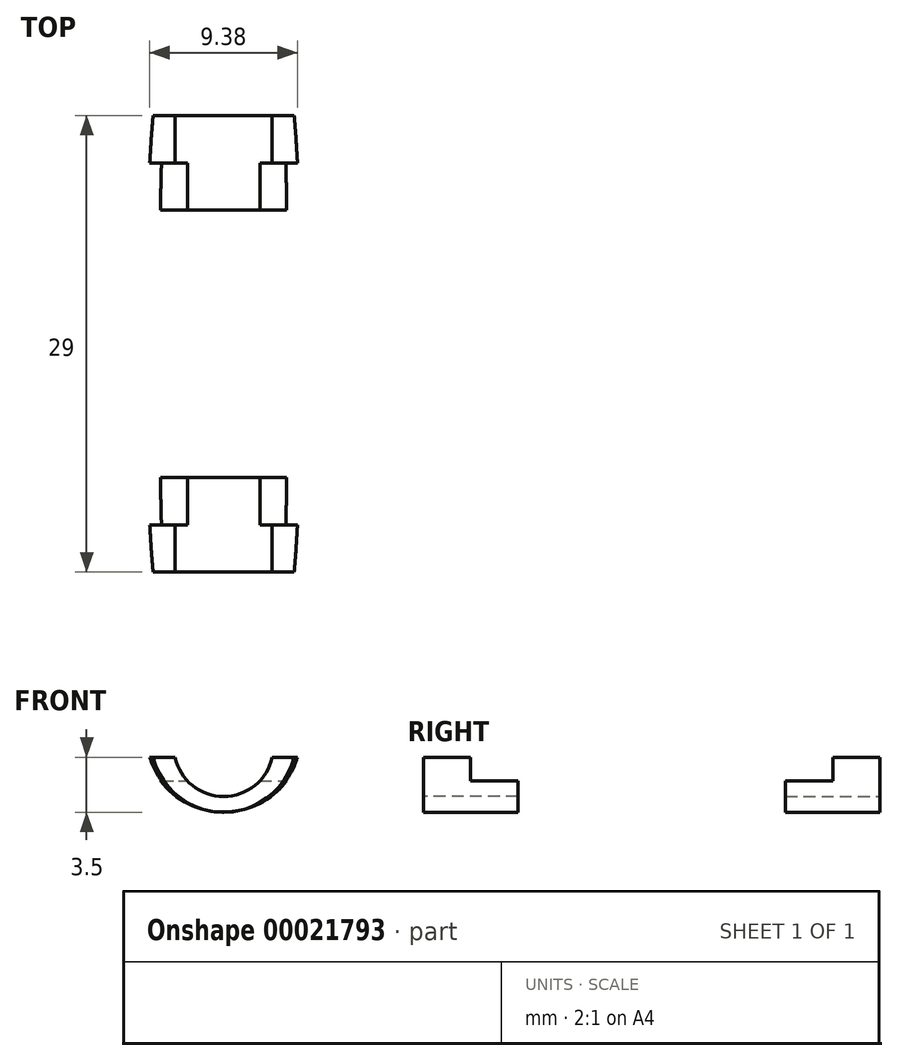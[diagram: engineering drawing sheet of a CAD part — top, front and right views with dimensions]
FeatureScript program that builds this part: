
annotation { "Feature Type Name" : "Feature", "Feature Type Description" : "" }
export const myFeature = defineFeature(function(context is Context, id is Id, definition is map)
    precondition{}
    {
        {
            var Q0;
            Q0=qCreatedBy(makeId("Top.planeOp"),FACE);
            var sketch = newSketch(context, id + "F0", { "sketchPlane" : qUnion([Q0])});
            skLineSegment(sketch, "E0.bottom", {"start": v(-2.4, 0) * mm, "end": v(2.4, 0) * mm, "construction": true});
            skLineSegment(sketch, "E0.top", {"start": v(-2.4, 4.6) * mm, "end": v(2.4, 4.6) * mm, "construction": true});
            skLineSegment(sketch, "E0.left", {"start": v(-2.4, 0) * mm, "end": v(-2.4, 4.6) * mm, "construction": true});
            skLineSegment(sketch, "E0.right", {"start": v(2.4, 0) * mm, "end": v(2.4, 4.6) * mm, "construction": true});
            skLineSegment(sketch, "E1", {"start": v(-1.27, 0) * mm, "end": v(-2, -1.5) * mm, "construction": true});
            skLineSegment(sketch, "E2", {"start": v(-2, -1.5) * mm, "end": v(-2, -14) * mm, "construction": true});
            skLineSegment(sketch, "E3", {"start": v(0, 0) * mm, "end": v(0, -14) * mm, "construction": true});
            skLineSegment(sketch, "E4", {"start": v(1.27, 0) * mm, "end": v(2, -1.5) * mm, "construction": true});
            skLineSegment(sketch, "E5", {"start": v(2, -1.5) * mm, "end": v(2, -14) * mm, "construction": true});
            skSolve(sketch);
        }
        {
            var Q0;
            Q0=qCreatedBy(makeId("Top.planeOp"),FACE);
            var sketch = newSketch(context, id + "F1", { "sketchPlane" : qUnion([Q0])});
            skLineSegment(sketch, "E6", {"start": v(2.4, -2.5) * mm, "end": v(1.6, -2.5) * mm});
            skLineSegment(sketch, "E7", {"start": v(1.6, -2.5) * mm, "end": v(1.6, -3.3) * mm});
            skLineSegment(sketch, "E8", {"start": v(1.6, -3.3) * mm, "end": v(0.4, -3.3) * mm});
            skLineSegment(sketch, "E9", {"start": v(0.4, -3.3) * mm, "end": v(0.4, -6.25) * mm});
            skLineSegment(sketch, "E10", {"start": v(0.4, -6.25) * mm, "end": v(-0.4, -6.25) * mm});
            skLineSegment(sketch, "E11", {"start": v(-0.4, -6.25) * mm, "end": v(-0.4, -7.05) * mm});
            skLineSegment(sketch, "E12", {"start": v(-0.4, -7.05) * mm, "end": v(-1.6, -7.05) * mm});
            skLineSegment(sketch, "E13", {"start": v(-1.6, -7.05) * mm, "end": v(-1.6, -10) * mm});
            skLineSegment(sketch, "E14", {"start": v(-1.6, -10) * mm, "end": v(-2.4, -10) * mm});
            skPoint(sketch, "E15", {"position": v(2, -2.5) * mm});
            skPoint(sketch, "E16", {"position": v(0, -6.25) * mm});
            skPoint(sketch, "E17", {"position": v(-2, -10) * mm});
            skLineSegment(sketch, "E18", {"start": v(-2.4, -10) * mm, "end": v(-2.4, -10.8) * mm});
            skLineSegment(sketch, "E19", {"start": v(-2.4, -10.8) * mm, "end": v(-7.4, -10.8) * mm});
            skLineSegment(sketch, "E20", {"start": v(-7.4, -10.8) * mm, "end": v(-7.4, 4.6) * mm});
            skLineSegment(sketch, "E21", {"start": v(2.4, -2.5) * mm, "end": v(2.4, -1.5) * mm});
            skLineSegment(sketch, "E22", {"start": v(2.4, -1.5) * mm, "end": v(-2.4, -1.5) * mm});
            skLineSegment(sketch, "E23", {"start": v(-2.4, -1.5) * mm, "end": v(-2.4, -10) * mm});
            skLineSegment(sketch, "E24", {"start": v(-1.6, -7.05) * mm, "end": v(-1.6, -1.5) * mm});
            skLineSegment(sketch, "E25", {"start": v(-0.4, -6.25) * mm, "end": v(-0.4, -1.5) * mm});
            skLineSegment(sketch, "E26", {"start": v(0.4, -3.3) * mm, "end": v(0.4, -1.5) * mm});
            skLineSegment(sketch, "E27", {"start": v(1.6, -2.5) * mm, "end": v(1.6, -1.5) * mm});
            skLineSegment(sketch, "E28", {"start": v(2.4, -2.5) * mm, "end": v(7.4, -2.5) * mm});
            skLineSegment(sketch, "E29", {"start": v(7.4, -2.5) * mm, "end": v(7.4, 4.6) * mm});
            skLineSegment(sketch, "E30", {"start": v(-7.4, -12) * mm, "end": v(-7.4, -10.9) * mm});
            skLineSegment(sketch, "E31", {"start": v(-7.4, -10.9) * mm, "end": v(-1.5, -10.9) * mm});
            skLineSegment(sketch, "E32", {"start": v(-1.5, -10.9) * mm, "end": v(-1.5, -7.15) * mm});
            skLineSegment(sketch, "E33", {"start": v(-1.5, -7.15) * mm, "end": v(0.5, -7.15) * mm});
            skLineSegment(sketch, "E34", {"start": v(0.5, -7.15) * mm, "end": v(0.5, -3.4) * mm});
            skLineSegment(sketch, "E35", {"start": v(0.5, -3.4) * mm, "end": v(2.4, -3.4) * mm});
            skLineSegment(sketch, "E36", {"start": v(2.4, -3.4) * mm, "end": v(2.4, -2.6) * mm});
            skLineSegment(sketch, "E37", {"start": v(2.4, -2.6) * mm, "end": v(7.4, -2.6) * mm});
            skLineSegment(sketch, "E38", {"start": v(7.4, -2.6) * mm, "end": v(7.4, -12) * mm});
            skLineSegment(sketch, "E39", {"start": v(-1.5, -7.15) * mm, "end": v(-1.5, -7.05) * mm, "construction": true});
            skLineSegment(sketch, "E40", {"start": v(-1.5, -7.15) * mm, "end": v(-1.6, -7.15) * mm, "construction": true});
            skLineSegment(sketch, "E41", {"start": v(-7.4, -10.9) * mm, "end": v(-7.4, -10.8) * mm, "construction": true});
            skLineSegment(sketch, "E42", {"start": v(0.5, -3.4) * mm, "end": v(0.4, -3.4) * mm, "construction": true});
            skLineSegment(sketch, "E43", {"start": v(0.5, -3.4) * mm, "end": v(0.5, -3.3) * mm, "construction": true});
            skLineSegment(sketch, "E44", {"start": v(2.4, -2.6) * mm, "end": v(2.4, -2.5) * mm, "construction": true});
            skLineSegment(sketch, "E45", {"start": v(-2.6, -0.2) * mm, "end": v(2.6, -0.2) * mm});
            skLineSegment(sketch, "E46", {"start": v(2.6, -0.2) * mm, "end": v(2.6, 4.6) * mm});
            skLineSegment(sketch, "E47", {"start": v(-2.6, -0.2) * mm, "end": v(-2.6, 4.6) * mm});
            skLineSegment(sketch, "E48", {"start": v(-2.6, 0) * mm, "end": v(-2.4, 0) * mm, "construction": true});
            skLineSegment(sketch, "E49", {"start": v(-2.4, 0) * mm, "end": v(-2.4, -0.2) * mm, "construction": true});
            skLineSegment(sketch, "E50", {"start": v(2.6, 0) * mm, "end": v(2.4, 0) * mm, "construction": true});
            skLineSegment(sketch, "E51", {"start": v(-7.4, 4.6) * mm, "end": v(-2.6, 4.6) * mm});
            skLineSegment(sketch, "E52", {"start": v(2.6, 4.6) * mm, "end": v(7.4, 4.6) * mm});
            skLineSegment(sketch, "E53", {"start": v(-7.4, -12) * mm, "end": v(7.4, -12) * mm});
            skLineSegment(sketch, "E54", {"start": v(2.4, -1.5) * mm, "end": v(2.6, -0.2) * mm});
            skLineSegment(sketch, "E55", {"start": v(-2.4, -1.5) * mm, "end": v(-2.6, -0.2) * mm});
            skLineSegment(sketch, "E56", {"start": v(-2.6, 4.6) * mm, "end": v(2.6, 4.6) * mm});
            skLineSegment(sketch, "E57", {"start": v(-7.4, -10.9) * mm, "end": v(-7.4, -10.8) * mm});
            skLineSegment(sketch, "E58", {"start": v(7.4, -2.6) * mm, "end": v(7.4, -2.5) * mm});
            skLineSegment(sketch, "E59", {"start": v(7.4, 4.6) * mm, "end": v(7.4, 5) * mm});
            skLineSegment(sketch, "E60", {"start": v(7.4, 5) * mm, "end": v(-7.4, 5) * mm});
            skLineSegment(sketch, "E61", {"start": v(-7.4, 5) * mm, "end": v(-7.4, 4.6) * mm});
            skLineSegment(sketch, "E62", {"start": v(7.4, -3.5) * mm, "end": v(-7.4, -3.5) * mm, "construction": true});
            skLineSegment(sketch, "E63", {"start": v(0, 5) * mm, "end": v(0, -12) * mm, "construction": true});
            skPoint(sketch, "E64", {"position": v(0, -3.5) * mm});
            skSolve(sketch);
        }
        {
            var Q0;
            Q0=qCreatedBy(makeId("Front.planeOp"),FACE);
            var sketch = newSketch(context, id + "F2", { "sketchPlane" : qUnion([Q0])});
            skCircle(sketch, "E65", {"center": v(0, 0) * mm, "radius": 3.15 * mm, "construction": true});
            skLineSegment(sketch, "E66", {"start": v(-2.4, 3.25) * mm, "end": v(2.4, 3.25) * mm, "construction": true});
            skLineSegment(sketch, "E67", {"start": v(2.4, 3.25) * mm, "end": v(2.4, 4.25) * mm, "construction": true});
            skLineSegment(sketch, "E68", {"start": v(-2.4, 3.25) * mm, "end": v(-2.4, 4.25) * mm, "construction": true});
            skPoint(sketch, "E69", {"position": v(0, 3.25) * mm});
            skArc(sketch, "E70", {"start": v(2.4, 4.25) * mm, "mid": v(0, 6.85) * mm, "end": v(-2.4, 4.25) * mm, "construction": true});
            skLineSegment(sketch, "E71", {"start": v(-2.4, 4.25) * mm, "end": v(2.4, 4.25) * mm, "construction": true});
            skCircle(sketch, "E72", {"center": v(0, -1.5) * mm, "radius": 1.25 * mm});
            skCircle(sketch, "E73", {"center": v(2.75, 1) * mm, "radius": 1.25 * mm});
            skCircle(sketch, "E74", {"center": v(-2.75, 1) * mm, "radius": 1.25 * mm});
            skLineSegment(sketch, "E75", {"start": v(1.6, 5.75) * mm, "end": v(1.6, 4.25) * mm});
            skLineSegment(sketch, "E76", {"start": v(1.6, 4.25) * mm, "end": v(2.4, 4.25) * mm});
            skLineSegment(sketch, "E77", {"start": v(2.4, 4.25) * mm, "end": v(2.4, 5.75) * mm});
            skLineSegment(sketch, "E78", {"start": v(2.4, 5.75) * mm, "end": v(3.13, 5.75) * mm});
            skLineSegment(sketch, "E79", {"start": v(1.6, 5.75) * mm, "end": v(0.5, 5.75) * mm});
            skLineSegment(sketch, "E80", {"start": v(0.5, 5.75) * mm, "end": v(0.5, 4.25) * mm});
            skLineSegment(sketch, "E81", {"start": v(0.5, 4.25) * mm, "end": v(-0.4, 4.25) * mm});
            skLineSegment(sketch, "E82", {"start": v(-0.4, 4.25) * mm, "end": v(-0.4, 5.75) * mm});
            skLineSegment(sketch, "E83", {"start": v(-0.4, 5.75) * mm, "end": v(-1.5, 5.75) * mm});
            skLineSegment(sketch, "E84", {"start": v(-1.5, 5.75) * mm, "end": v(-1.5, 4.25) * mm});
            skLineSegment(sketch, "E85", {"start": v(-1.5, 4.25) * mm, "end": v(-2.4, 4.25) * mm});
            skLineSegment(sketch, "E86", {"start": v(-2.4, 4.25) * mm, "end": v(-2.4, 5.75) * mm});
            skLineSegment(sketch, "E87", {"start": v(-2.4, 5.75) * mm, "end": v(-3.13, 5.75) * mm});
            skLineSegment(sketch, "E88", {"start": v(2.75, 1) * mm, "end": v(0, 1) * mm, "construction": true});
            skLineSegment(sketch, "E89", {"start": v(0, 1) * mm, "end": v(-2.75, 1) * mm, "construction": true});
            skLineSegment(sketch, "E90", {"start": v(-2.4, 4.25) * mm, "end": v(-2.4, 2.2) * mm});
            skLineSegment(sketch, "E91", {"start": v(-1.5, 4.25) * mm, "end": v(-1.5, 1) * mm});
            skLineSegment(sketch, "E92", {"start": v(-0.4, 4.25) * mm, "end": v(-0.4, -0.32) * mm});
            skLineSegment(sketch, "E93", {"start": v(0.5, 4.25) * mm, "end": v(0.5, -0.35) * mm});
            skLineSegment(sketch, "E94", {"start": v(1.6, 4.25) * mm, "end": v(1.6, 1.49) * mm});
            skLineSegment(sketch, "E95", {"start": v(2.4, 4.25) * mm, "end": v(2.4, 2.2) * mm});
            skLineSegment(sketch, "E96", {"start": v(2.4, 5.75) * mm, "end": v(1.6, 5.75) * mm});
            skLineSegment(sketch, "E97", {"start": v(0.5, 5.75) * mm, "end": v(-0.4, 5.75) * mm});
            skLineSegment(sketch, "E98", {"start": v(-1.5, 5.75) * mm, "end": v(-2.4, 5.75) * mm});
            skLineSegment(sketch, "E99", {"start": v(-1.5, 4.25) * mm, "end": v(-0.4, 4.25) * mm});
            skLineSegment(sketch, "E100", {"start": v(0.5, 4.25) * mm, "end": v(1.6, 4.25) * mm});
            skLineSegment(sketch, "E101", {"start": v(-4.1, 5) * mm, "end": v(-4.84, 2.1) * mm});
            skLineSegment(sketch, "E102", {"start": v(4.1, 5) * mm, "end": v(4.84, 2.1) * mm});
            skArc(sketch, "E103", {"start": v(-4.84, 2.1) * mm, "mid": v(0, -4.15) * mm, "end": v(4.84, 2.1) * mm});
            skLineSegment(sketch, "E104", {"start": v(-1.14, -0.99) * mm, "end": v(-1.5, 1) * mm});
            skLineSegment(sketch, "E105", {"start": v(-1.61, 0.49) * mm, "end": v(-1.25, -1.5) * mm});
            skLineSegment(sketch, "E106", {"start": v(1.25, -1.5) * mm, "end": v(1.61, 0.49) * mm});
            skLineSegment(sketch, "E107", {"start": v(1.5, 1) * mm, "end": v(1.14, -0.99) * mm});
            skLineSegment(sketch, "E108", {"start": v(-4, 1) * mm, "end": v(-5, 1) * mm});
            skLineSegment(sketch, "E109", {"start": v(4, 1) * mm, "end": v(5, 1) * mm});
            skLineSegment(sketch, "E110", {"start": v(4, 0.9) * mm, "end": v(5, 0.9) * mm});
            skLineSegment(sketch, "E111", {"start": v(-4, 0.9) * mm, "end": v(-5, 0.9) * mm});
            skPoint(sketch, "E112.visualSharp", {"position": v(-3.9, 5.75) * mm});
            skArc(sketch, "E112.filletArc", {"start": v(-3.13, 5.75) * mm, "mid": v(-3.74, 5.54) * mm, "end": v(-4.1, 5) * mm});
            skPoint(sketch, "E113.visualSharp", {"position": v(3.9, 5.75) * mm});
            skArc(sketch, "E113.filletArc", {"start": v(4.1, 5) * mm, "mid": v(3.74, 5.54) * mm, "end": v(3.13, 5.75) * mm});
            skSolve(sketch);
        }
        {
            var Q0;
            Q0=sQuery(id+"F1.wireOp",VERTEX,"E45.end");
            var Q1;
            Q1=qCreatedBy(makeId("Front.planeOp"),FACE);
            cPlane(context, id + "F3", {"entities" : qUnion([Q0, Q1]), "cplaneType" : CPlaneType.PLANE_POINT, "offset" : 150 * mm, "width" : 150 * mm, "height" : 150 * mm});
        }
        {
            var Q0;
            Q0=qCreatedBy(makeId("Front.planeOp"),FACE);
            var Q1;
            Q1=sQuery(id+"F1.wireOp",VERTEX,"E21.end");
            cPlane(context, id + "F4", {"entities" : qUnion([Q0, Q1]), "cplaneType" : CPlaneType.PLANE_POINT, "offset" : 150 * mm, "width" : 150 * mm, "height" : 150 * mm});
        }
        {
            var Q0;
            Q0=qCreatedBy(id+"F3.planeOp",FACE);
            var sketch = newSketch(context, id + "F5", { "sketchPlane" : qUnion([Q0])});
            skLineSegment(sketch, "E114.0", {"start": v(-2.4, 3.25) * mm, "end": v(2.4, 3.25) * mm});
            skLineSegment(sketch, "E115", {"start": v(-2.4, 3.25) * mm, "end": v(-2.4, 6.25) * mm});
            skLineSegment(sketch, "E116", {"start": v(2.4, 3.25) * mm, "end": v(2.4, 6.25) * mm});
            skLineSegment(sketch, "E117", {"start": v(2.4, 6.25) * mm, "end": v(-2.4, 6.25) * mm});
            skSolve(sketch);
        }
        {
            var Q0;
            Q0=makeQuery(id+"F2.imprint","IMPRINT",FACE,{"disambiguationData":[TD([[makeQuery(id+"F2.imprint","IMPRINT",EDGE,{"derivedFrom":sQuery(id+"F2.wireOp",EDGE,"E86")}),1.0]])]});
            var Q1;
            Q1=makeQuery(id+"F2.imprint","IMPRINT",FACE,{"disambiguationData":[TD([[makeQuery(id+"F2.imprint","IMPRINT",EDGE,{"derivedFrom":sQuery(id+"F2.wireOp",EDGE,"E85")}),1.0]])]});
            var Q2;
            Q2=makeQuery(id+"F2.imprint","IMPRINT",FACE,{"disambiguationData":[TD([[makeQuery(id+"F2.imprint","IMPRINT",EDGE,{"derivedFrom":sQuery(id+"F2.wireOp",EDGE,"E82")}),1.0]])]});
            var Q3;
            Q3=makeQuery(id+"F2.imprint","IMPRINT",FACE,{"disambiguationData":[TD([[makeQuery(id+"F2.imprint","IMPRINT",EDGE,{"derivedFrom":sQuery(id+"F2.wireOp",EDGE,"E81")}),1.0]])]});
            var Q4;
            Q4=makeQuery(id+"F2.imprint","IMPRINT",FACE,{"disambiguationData":[TD([[makeQuery(id+"F2.imprint","IMPRINT",EDGE,{"derivedFrom":sQuery(id+"F2.wireOp",EDGE,"E75")}),-1.0]])]});
            var Q5;
            Q5=makeQuery(id+"F2.imprint","IMPRINT",FACE,{"disambiguationData":[TD([[makeQuery(id+"F2.imprint","IMPRINT",EDGE,{"derivedFrom":sQuery(id+"F2.wireOp",EDGE,"E76")}),-1.0]])]});
            var Q6;
            Q6=makeQuery(id+"F2.imprint","IMPRINT",FACE,{"disambiguationData":[TD([[makeQuery(id+"F2.imprint","IMPRINT",EDGE,{"derivedFrom":sQuery(id+"F2.wireOp",EDGE,"E77")}),-1.0]])]});
            var Q7;
            {var subQ3=sQuery(id+"F2.wireOp",EDGE,"41fa8a35-a4bc-480c-a0cd-76908c7cfabe");Q7=makeQuery(id+"F2.imprint","IMPRINT",FACE,{"disambiguationData":[TD([[makeQuery(id+"F2.imprint","IMPRINT",EDGE,{"derivedFrom":subQ3}),1.0]])]});}
            var Q8;
            Q8=makeQuery(id+"F2.imprint","IMPRINT",FACE,{"disambiguationData":[TD([[makeQuery(id+"F2.imprint","IMPRINT",EDGE,{"derivedFrom":sQuery(id+"F2.wireOp",EDGE,"E84")}),-1.0]])]});
            var Q9;
            Q9=makeQuery(id+"F2.imprint","IMPRINT",FACE,{"disambiguationData":[TD([[makeQuery(id+"F2.imprint","IMPRINT",EDGE,{"derivedFrom":sQuery(id+"F2.wireOp",EDGE,"E80")}),-1.0]])]});
            var Q10;
            Q10=makeQuery(id+"F2.imprint","IMPRINT",FACE,{"disambiguationData":[TD([[makeQuery(id+"F2.imprint","IMPRINT",EDGE,{"derivedFrom":sQuery(id+"F2.wireOp",EDGE,"E75")}),1.0]])]});
            var Q11;
            {var subQ2=sQuery(id+"F2.wireOp",EDGE,"E93");Q11=makeQuery(id+"F2.imprint","IMPRINT",FACE,{"disambiguationData":[TD([[makeQuery(id+"F2.imprint","IMPRINT",EDGE,{"derivedFrom":subQ2}),1.0]])]});}
            var Q12;
            {var subQ2=sQuery(id+"F2.wireOp",EDGE,"E91");Q12=makeQuery(id+"F2.imprint","IMPRINT",FACE,{"disambiguationData":[TD([[makeQuery(id+"F2.imprint","IMPRINT",EDGE,{"derivedFrom":subQ2}),1.0]])]});}
            var Q13;
            {var subQ1=sQuery(id+"F2.wireOp",EDGE,"E105");Q13=makeQuery(id+"F2.imprint","IMPRINT",FACE,{"disambiguationData":[TD([[makeQuery(id+"F2.imprint","IMPRINT",EDGE,{"derivedFrom":subQ1}),-1.0]])]});}
            extrude(context, id + "F6", {"entities" : qUnion([Q0, Q1, Q2, Q3, Q4, Q5, Q6, Q7, Q8, Q9, Q10, Q11, Q12, Q13]), "depth" : 12 * mm, "hasSecondDirection" : true, "secondDirectionOppositeDirection" : true, "secondDirectionDepth" : 5 * mm});
        }
        {
            var Q0;
            Q0=makeQuery(id+"F1.imprint","IMPRINT",FACE,{"disambiguationData":[TD([[makeQuery(id+"F1.imprint","IMPRINT",EDGE,{"derivedFrom":sQuery(id+"F1.wireOp",EDGE,"E18")}),-1.0]])]});
            var Q1;
            Q1=makeQuery(id+"F1.imprint","IMPRINT",FACE,{"disambiguationData":[TD([[makeQuery(id+"F1.imprint","IMPRINT",EDGE,{"derivedFrom":sQuery(id+"F1.wireOp",EDGE,"E13")}),-1.0]])]});
            var Q2;
            Q2=makeQuery(id+"F1.imprint","IMPRINT",FACE,{"disambiguationData":[TD([[makeQuery(id+"F1.imprint","IMPRINT",EDGE,{"derivedFrom":sQuery(id+"F1.wireOp",EDGE,"E11")}),-1.0]])]});
            var Q3;
            Q3=makeQuery(id+"F1.imprint","IMPRINT",FACE,{"disambiguationData":[TD([[makeQuery(id+"F1.imprint","IMPRINT",EDGE,{"derivedFrom":sQuery(id+"F1.wireOp",EDGE,"E9")}),-1.0]])]});
            var Q4;
            Q4=makeQuery(id+"F1.imprint","IMPRINT",FACE,{"disambiguationData":[TD([[makeQuery(id+"F1.imprint","IMPRINT",EDGE,{"derivedFrom":sQuery(id+"F1.wireOp",EDGE,"E7")}),-1.0]])]});
            var Q5;
            Q5=makeQuery(id+"F1.imprint","IMPRINT",FACE,{"disambiguationData":[TD([[makeQuery(id+"F1.imprint","IMPRINT",EDGE,{"derivedFrom":sQuery(id+"F1.wireOp",EDGE,"E6")}),-1.0]])]});
            var Q6;
            Q6=makeQuery(id+"F1.imprint","IMPRINT",FACE,{"disambiguationData":[TD([[makeQuery(id+"F1.imprint","IMPRINT",EDGE,{"derivedFrom":sQuery(id+"F1.wireOp",EDGE,"E21")}),-1.0]])]});
            var Q7;
            Q7=makeQuery(id+"F1.imprint","IMPRINT",FACE,{"disambiguationData":[TD([[makeQuery(id+"F1.imprint","IMPRINT",EDGE,{"derivedFrom":sQuery(id+"F1.wireOp",EDGE,"E45")}),-1.0]])]});
            var Q8;
            Q8=makeQuery(id+"F1.imprint","IMPRINT",FACE,{"disambiguationData":[TD([[makeQuery(id+"F1.imprint","IMPRINT",EDGE,{"derivedFrom":sQuery(id+"F1.wireOp",EDGE,"E45")}),1.0]])]});
            var Q9;
            Q9=makeQuery(id+"F1.imprint","IMPRINT",FACE,{"disambiguationData":[TD([[makeQuery(id+"F1.imprint","IMPRINT",EDGE,{"derivedFrom":sQuery(id+"F1.wireOp",EDGE,"E30")}),-1.0]])]});
            var Q10;
            Q10=makeQuery(id+"F1.imprint","IMPRINT",FACE,{"disambiguationData":[TD([[makeQuery(id+"F1.imprint","IMPRINT",EDGE,{"derivedFrom":sQuery(id+"F1.wireOp",EDGE,"E51")}),1.0]])]});
            extrude(context, id + "F7", {"entities" : qUnion([Q0, Q1, Q2, Q3, Q4, Q5, Q6, Q7, Q8, Q9, Q10]), "operationType" : NewBodyOperationType.INTERSECT, "depth" : 25 * mm, "hasSecondDirection" : true, "secondDirectionOppositeDirection" : true, "secondDirectionDepth" : 25 * mm});
        }
        {
            var Q0;
            Q0=makeQuery(id+"F2.imprint","IMPRINT",FACE,{"disambiguationData":[TD([[makeQuery(id+"F2.imprint","IMPRINT",EDGE,{"derivedFrom":sQuery(id+"F2.wireOp",EDGE,"E84")}),-1.0]])]});
            var Q1;
            Q1=makeQuery(id+"F2.imprint","IMPRINT",FACE,{"disambiguationData":[TD([[makeQuery(id+"F2.imprint","IMPRINT",EDGE,{"derivedFrom":sQuery(id+"F2.wireOp",EDGE,"E80")}),-1.0]])]});
            var Q2;
            Q2=makeQuery(id+"F2.imprint","IMPRINT",FACE,{"disambiguationData":[TD([[makeQuery(id+"F2.imprint","IMPRINT",EDGE,{"derivedFrom":sQuery(id+"F2.wireOp",EDGE,"E75")}),1.0]])]});
            var Q3;
            Q3=qCreatedBy(id+"F3.planeOp",FACE);
            extrude(context, id + "F8", {"entities" : qUnion([Q0, Q1, Q2]), "operationType" : NewBodyOperationType.REMOVE, "endBoundEntityFace" : qUnion([Q3]), "depth" : 25 * mm});
        }
        {
            var Q0;
            Q0=makeQuery(id+"F2.imprint","IMPRINT",FACE,{"disambiguationData":[TD([[makeQuery(id+"F2.imprint","IMPRINT",EDGE,{"derivedFrom":sQuery(id+"F2.wireOp",EDGE,"E84")}),-1.0]])]});
            var Q1;
            Q1=makeQuery(id+"F2.imprint","IMPRINT",FACE,{"disambiguationData":[TD([[makeQuery(id+"F2.imprint","IMPRINT",EDGE,{"derivedFrom":sQuery(id+"F2.wireOp",EDGE,"E82")}),1.0]])]});
            var Q2;
            Q2=makeQuery(id+"F2.imprint","IMPRINT",FACE,{"disambiguationData":[TD([[makeQuery(id+"F2.imprint","IMPRINT",EDGE,{"derivedFrom":sQuery(id+"F2.wireOp",EDGE,"E80")}),-1.0]])]});
            var Q3;
            Q3=makeQuery(id+"F2.imprint","IMPRINT",FACE,{"disambiguationData":[TD([[makeQuery(id+"F2.imprint","IMPRINT",EDGE,{"derivedFrom":sQuery(id+"F2.wireOp",EDGE,"E75")}),-1.0]])]});
            var Q4;
            Q4=makeQuery(id+"F2.imprint","IMPRINT",FACE,{"disambiguationData":[TD([[makeQuery(id+"F2.imprint","IMPRINT",EDGE,{"derivedFrom":sQuery(id+"F2.wireOp",EDGE,"E75")}),1.0]])]});
            var Q5;
            Q5=qCreatedBy(id+"F4.planeOp",FACE);
            extrude(context, id + "F9", {"entities" : qUnion([Q0, Q1, Q2, Q3, Q4]), "operationType" : NewBodyOperationType.REMOVE, "endBound" : BoundingType.UP_TO_SURFACE, "endBoundEntityFace" : qUnion([Q5]), "depth" : 25 * mm});
        }
        {
            var Q0;
            Q0 = qSketchRegion(id + "F5", true);
            extrude(context, id + "F10", {"entities" : qUnion([Q0]), "operationType" : NewBodyOperationType.REMOVE, "oppositeDirection" : true, "depth" : 25 * mm});
        }
        {
            var Q0;
            {var subQ0=sQuery(id+"F2.wireOp",EDGE,"E76");var subQ1=sQuery(id+"F2.wireOp",EDGE,"E81");var subQ2=sQuery(id+"F2.wireOp",EDGE,"E85");Q0=makeQuery(id+"F10.boolean.opBoolean","INTERSECT",EDGE,{"derivedFrom":[makeQuery(id+"F9.boolean.opBoolean","MERGE",FACE,{"derivedFrom":[makeQuery(id+"F8.boolean.opBoolean","COPY",FACE,{"derivedFrom":makeQuery(id+"F8.opExtrude","SWEPT_FACE",FACE,{"disambiguationData":[OSD([subQ0])]})}),makeQuery(id+"F8.boolean.opBoolean","COPY",FACE,{"derivedFrom":makeQuery(id+"F8.opExtrude","SWEPT_FACE",FACE,{"disambiguationData":[OSD([subQ1])]})}),makeQuery(id+"F8.boolean.opBoolean","COPY",FACE,{"derivedFrom":makeQuery(id+"F8.opExtrude","SWEPT_FACE",FACE,{"disambiguationData":[OSD([subQ2])]})}),makeQuery(id+"F9.opExtrude","SWEPT_FACE",FACE,{"disambiguationData":[OSD([subQ0,subQ1,subQ2,sQuery(id+"F2.wireOp",EDGE,"E99"),sQuery(id+"F2.wireOp",EDGE,"E100")])]})]}),makeQuery(id+"F10.opExtrude","CAP_FACE",FACE,{"disambiguationData":[OSD([sQuery(id+"F5.wireOp",EDGE,"E114.0"),sQuery(id+"F5.wireOp",EDGE,"E115"),sQuery(id+"F5.wireOp",EDGE,"E116"),sQuery(id+"F5.wireOp",EDGE,"E117")])],"isStart":true})]});}
            chamfer(context, id + "F11", {"entities" : qUnion([Q0]), "chamferType" : ChamferType.OFFSET_ANGLE, "width" : 1.5 * mm, "oppositeDirection" : true, "angle" : 30 * degree, "tangentPropagation" : true});
        }
        {
            var Q0;
            Q0=makeQuery(id+"F9.boolean.opBoolean","COPY",EDGE,{"disambiguationData":[OD(0.0)],"derivedFrom":makeQuery(id+"F9.opExtrude","CAP_EDGE",EDGE,{"disambiguationData":[OSD([sQuery(id+"F2.wireOp",EDGE,"E79"),sQuery(id+"F2.wireOp",EDGE,"E83"),sQuery(id+"F2.wireOp",EDGE,"E96"),sQuery(id+"F2.wireOp",EDGE,"E97"),sQuery(id+"F2.wireOp",EDGE,"E98")])],"isStart":false})});
            var Q1;
            Q1=makeQuery(id+"F9.boolean.opBoolean","COPY",EDGE,{"disambiguationData":[OD(1.0)],"derivedFrom":makeQuery(id+"F9.opExtrude","CAP_EDGE",EDGE,{"disambiguationData":[OSD([sQuery(id+"F2.wireOp",EDGE,"E79"),sQuery(id+"F2.wireOp",EDGE,"E83"),sQuery(id+"F2.wireOp",EDGE,"E96"),sQuery(id+"F2.wireOp",EDGE,"E97"),sQuery(id+"F2.wireOp",EDGE,"E98")])],"isStart":false})});
            chamfer(context, id + "F12", {"entities" : qUnion([Q0, Q1]), "chamferType" : ChamferType.OFFSET_ANGLE, "width" : 1.5 * mm, "oppositeDirection" : true, "angle" : 30 * degree, "tangentPropagation" : true});
        }
        {
            var Q0;
            Q0=makeQuery(id+"F6.opExtrude","CAP_FACE",FACE,{"disambiguationData":[OSD([sQuery(id+"F2.wireOp",EDGE,"E72"),sQuery(id+"F2.wireOp",EDGE,"E73"),sQuery(id+"F2.wireOp",EDGE,"E74"),sQuery(id+"F2.wireOp",EDGE,"E78"),sQuery(id+"F2.wireOp",EDGE,"E79"),sQuery(id+"F2.wireOp",EDGE,"E83"),sQuery(id+"F2.wireOp",EDGE,"E87"),sQuery(id+"F2.wireOp",EDGE,"E96"),sQuery(id+"F2.wireOp",EDGE,"E97"),sQuery(id+"F2.wireOp",EDGE,"E98"),sQuery(id+"F2.wireOp",EDGE,"E101"),sQuery(id+"F2.wireOp",EDGE,"E102"),sQuery(id+"F2.wireOp",EDGE,"E103"),sQuery(id+"F2.wireOp",EDGE,"E104"),sQuery(id+"F2.wireOp",EDGE,"E107"),sQuery(id+"F2.wireOp",EDGE,"E108"),sQuery(id+"F2.wireOp",EDGE,"E109")])],"isStart":false});
            cPlane(context, id + "F13", {"entities" : qUnion([Q0]), "cplaneType" : CPlaneType.OFFSET, "offset" : 0 * mm, "width" : 150 * mm, "height" : 150 * mm});
        }
        {
            var Q0;
            Q0=qCreatedBy(id+"F13.planeOp",FACE);
            var sketch = newSketch(context, id + "F14", { "sketchPlane" : qUnion([Q0])});
            skCircle(sketch, "E118.0", {"center": v(2.75, 1) * mm, "radius": 1.25 * mm, "construction": true});
            skCircle(sketch, "E119.0", {"center": v(0, -1.5) * mm, "radius": 1.25 * mm, "construction": true});
            skCircle(sketch, "E120.0", {"center": v(-2.75, 1) * mm, "radius": 1.25 * mm, "construction": true});
            skLineSegment(sketch, "E121", {"start": v(-3.6, 0.08) * mm, "end": v(-0.84, -2.42) * mm});
            skLineSegment(sketch, "E122", {"start": v(0.84, -2.42) * mm, "end": v(3.6, 0.08) * mm});
            skLineSegment(sketch, "E123", {"start": v(2.75, 2.25) * mm, "end": v(-2.75, 2.25) * mm});
            skArc(sketch, "E124", {"start": v(-2.75, 2.25) * mm, "mid": v(-3.92, 1.45) * mm, "end": v(-3.6, 0.08) * mm});
            skArc(sketch, "E125", {"start": v(-0.84, -2.42) * mm, "mid": v(0, -2.75) * mm, "end": v(0.84, -2.42) * mm});
            skArc(sketch, "E126", {"start": v(3.6, 0.08) * mm, "mid": v(3.92, 1.45) * mm, "end": v(2.75, 2.25) * mm});
            skSolve(sketch);
        }
        {
            var Q0;
            Q0=makeQuery(id+"F6.opExtrude","CAP_FACE",FACE,{"disambiguationData":[OSD([sQuery(id+"F2.wireOp",EDGE,"E72"),sQuery(id+"F2.wireOp",EDGE,"E73"),sQuery(id+"F2.wireOp",EDGE,"E74"),sQuery(id+"F2.wireOp",EDGE,"E103"),sQuery(id+"F2.wireOp",EDGE,"E105"),sQuery(id+"F2.wireOp",EDGE,"E106"),sQuery(id+"F2.wireOp",EDGE,"E110"),sQuery(id+"F2.wireOp",EDGE,"E111")])],"isStart":false});
            cPlane(context, id + "F15", {"entities" : qUnion([Q0]), "cplaneType" : CPlaneType.OFFSET, "offset" : 6 * mm, "width" : 150 * mm, "height" : 150 * mm});
        }
        {
            var Q0;
            Q0=qCreatedBy(id+"F15.planeOp",FACE);
            var sketch = newSketch(context, id + "F16", { "sketchPlane" : qUnion([Q0])});
            skCircle(sketch, "E127.0", {"center": v(0, -1.5) * mm, "radius": 1.25 * mm, "construction": true});
            skArc(sketch, "E128", {"start": v(1.25, -1.25) * mm, "mid": v(2.5, 0) * mm, "end": v(1.25, 1.25) * mm});
            skArc(sketch, "E129", {"start": v(-1.25, 1.25) * mm, "mid": v(-2.5, 0) * mm, "end": v(-1.25, -1.25) * mm});
            skLineSegment(sketch, "E130", {"start": v(-1.25, 1.25) * mm, "end": v(1.25, 1.25) * mm});
            skLineSegment(sketch, "E131", {"start": v(1.25, -1.25) * mm, "end": v(1.05, -1.25) * mm});
            skLineSegment(sketch, "E132", {"start": v(-1.05, -1.25) * mm, "end": v(-1.25, -1.25) * mm});
            skLineSegment(sketch, "E133", {"start": v(1.05, -1.25) * mm, "end": v(-1.05, -1.25) * mm});
            skSolve(sketch);
        }
        {
            var Q0;
            Q0=qCreatedBy(id+"F15.planeOp",FACE);
            var sketch = newSketch(context, id + "F17", { "sketchPlane" : qUnion([Q0])});
            skCircle(sketch, "E134", {"center": v(0, 0) * mm, "radius": 3.15 * mm});
            skSolve(sketch);
        }
        {
            var Q0;
            Q0=qCreatedBy(id+"F15.planeOp",FACE);
            cPlane(context, id + "F18", {"entities" : qUnion([Q0]), "cplaneType" : CPlaneType.OFFSET, "offset" : 4 * mm, "width" : 150 * mm, "height" : 150 * mm});
        }
        {
            var Q0;
            Q0=qCreatedBy(id+"F13.planeOp",FACE);
            var sketch = newSketch(context, id + "F19", { "sketchPlane" : qUnion([Q0])});
            skArc(sketch, "E135.0", {"start": v(-4.84, 2.1) * mm, "mid": v(0, -4.15) * mm, "end": v(4.84, 2.1) * mm});
            skLineSegment(sketch, "E136.0", {"start": v(-4.1, 5) * mm, "end": v(-4.84, 2.1) * mm});
            skArc(sketch, "E137.0", {"start": v(-3.13, 5.75) * mm, "mid": v(-3.74, 5.54) * mm, "end": v(-4.1, 5) * mm});
            skArc(sketch, "E138.0", {"start": v(4.1, 5) * mm, "mid": v(3.74, 5.54) * mm, "end": v(3.13, 5.75) * mm});
            skLineSegment(sketch, "E139.0", {"start": v(4.1, 5) * mm, "end": v(4.84, 2.1) * mm});
            skLineSegment(sketch, "E140", {"start": v(3.13, 5.75) * mm, "end": v(-3.13, 5.75) * mm});
            skSolve(sketch);
        }
        {
            var Q0;
            Q0=qCreatedBy(id+"F18.planeOp",FACE);
            var sketch = newSketch(context, id + "F20", { "sketchPlane" : qUnion([Q0])});
            skArc(sketch, "E141", {"start": v(-3.8, 1.66) * mm, "mid": v(3.06, -2.8) * mm, "end": v(-1.98, 3.65) * mm});
            skArc(sketch, "E142", {"start": v(-2.63, 3.21) * mm, "mid": v(-3.3, 2.5) * mm, "end": v(-3.8, 1.66) * mm});
            skArc(sketch, "E143", {"start": v(-1.98, 3.65) * mm, "mid": v(-2.32, 3.44) * mm, "end": v(-2.63, 3.21) * mm});
            skLineSegment(sketch, "E144", {"start": v(-1.98, 3.65) * mm, "end": v(0, 0) * mm, "construction": true});
            skLineSegment(sketch, "E145", {"start": v(-2.63, 3.21) * mm, "end": v(0, 0) * mm, "construction": true});
            skLineSegment(sketch, "E146", {"start": v(-3.8, 1.66) * mm, "end": v(0, 0) * mm, "construction": true});
            skLineSegment(sketch, "E147.MirrorCS", {"start": v(1.98, 3.65) * mm, "end": v(0, 0) * mm, "construction": true});
            skLineSegment(sketch, "E148.MirrorCS", {"start": v(2.63, 3.21) * mm, "end": v(0, 0) * mm, "construction": true});
            skLineSegment(sketch, "E149.MirrorCS", {"start": v(3.8, 1.66) * mm, "end": v(0, 0) * mm, "construction": true});
            skSolve(sketch);
        }
        {
            var Q0;
            Q0=makeQuery(id+"F19.imprint","IMPRINT",FACE,{"disambiguationData":[TD([[makeQuery(id+"F19.imprint","IMPRINT",EDGE,{"derivedFrom":sQuery(id+"F19.wireOp",EDGE,"E135.0")}),1.0]])]});
            var Q1;
            Q1=makeQuery(id+"F20.imprint","IMPRINT",FACE,{"disambiguationData":[TD([[makeQuery(id+"F20.imprint","IMPRINT",EDGE,{"derivedFrom":sQuery(id+"F20.wireOp",EDGE,"E141")}),1.0]])]});
            var Q2;
            Q2=sQuery(id+"F20.wireOp",VERTEX,"E149.MirrorCS.start");
            var Q3;
            Q3=sQuery(id+"F19.wireOp",VERTEX,"E139.0.end");
            loft(context, id + "F21", {"startCondition" : LoftEndDerivativeType.NORMAL_TO_PROFILE, "startMagnitude" : 1, "sheetProfilesArray" : [{ "sheetProfileEntities" : qUnion([Q0]) }, { "sheetProfileEntities" : qUnion([Q1]) }], "matchConnections" : true, "connections" : [{ "connectionEntities" : qUnion([Q2, Q3]), "connectionEdgeQueries" : qUnion([]), "connectionEdgeParameters" : [] }]});
        }
        {
            var Q1;
            Q1=makeQuery(id+"F14.imprint","IMPRINT",FACE,{"disambiguationData":[TD([[makeQuery(id+"F14.imprint","IMPRINT",EDGE,{"derivedFrom":sQuery(id+"F14.wireOp",EDGE,"E121")}),1.0]])]});
            var Q2;
            Q2=makeQuery(id+"F16.imprint","IMPRINT",FACE,{"disambiguationData":[TD([[makeQuery(id+"F16.imprint","IMPRINT",EDGE,{"derivedFrom":sQuery(id+"F16.wireOp",EDGE,"E128")}),1.0]])]});
            loft(context, id + "F22", {"operationType" : NewBodyOperationType.REMOVE, "endCondition" : LoftEndDerivativeType.NORMAL_TO_PROFILE, "endMagnitude" : 1, "sheetProfilesArray" : [{ "sheetProfileEntities" : qUnion([Q1]) }, { "sheetProfileEntities" : qUnion([Q2]) }]});
        }
        {
            var Q0;
            Q0=qCreatedBy(id+"F18.planeOp",FACE);
            var sketch = newSketch(context, id + "F23", { "sketchPlane" : qUnion([Q0])});
            skLineSegment(sketch, "E150.rect.bottom", {"start": v(3.75, -1.5) * mm, "end": v(-3.75, -1.5) * mm});
            skLineSegment(sketch, "E150.rect.top", {"start": v(3.75, 1.5) * mm, "end": v(-3.75, 1.5) * mm});
            skLineSegment(sketch, "E150.rect.left", {"start": v(4.75, -0.5) * mm, "end": v(4.75, 0.5) * mm});
            skLineSegment(sketch, "E150.rect.right", {"start": v(-4.75, -0.5) * mm, "end": v(-4.75, 0.5) * mm});
            skPoint(sketch, "E150.rect.middle", {"position": v(0, 0) * mm});
            skPoint(sketch, "E151.visualSharp", {"position": v(-4.75, 1.5) * mm});
            skArc(sketch, "E151.filletArc", {"start": v(-3.75, 1.5) * mm, "mid": v(-4.46, 1.2) * mm, "end": v(-4.75, 0.5) * mm});
            skPoint(sketch, "E152.visualSharp", {"position": v(4.75, 1.5) * mm});
            skArc(sketch, "E152.filletArc", {"start": v(4.75, 0.5) * mm, "mid": v(4.46, 1.2) * mm, "end": v(3.75, 1.5) * mm});
            skPoint(sketch, "E153.visualSharp", {"position": v(-4.75, -1.5) * mm});
            skArc(sketch, "E153.filletArc", {"start": v(-4.75, -0.5) * mm, "mid": v(-4.46, -1.2) * mm, "end": v(-3.75, -1.5) * mm});
            skPoint(sketch, "E154.visualSharp", {"position": v(4.75, -1.5) * mm});
            skArc(sketch, "E154.filletArc", {"start": v(3.75, -1.5) * mm, "mid": v(4.46, -1.2) * mm, "end": v(4.75, -0.5) * mm});
            skSolve(sketch);
        }
        {
            var Q0;
            Q0 = qSketchRegion(id + "F19", true);
            var Q1;
            Q1=makeQuery(id+"F23.imprint","IMPRINT",FACE,{"disambiguationData":[TD([[makeQuery(id+"F23.imprint","IMPRINT",EDGE,{"derivedFrom":sQuery(id+"F23.wireOp",EDGE,"E150.rect.bottom")}),-1.0]])]});
            var Q2;
            Q2=sQuery(id+"F23.wireOp",VERTEX,"E153.filletArc.start");
            var Q3;
            Q3=sQuery(id+"F19.wireOp",VERTEX,"E136.0.end");
            loft(context, id + "F24", {"startCondition" : LoftEndDerivativeType.NORMAL_TO_PROFILE, "startMagnitude" : 0.5, "sheetProfilesArray" : [{ "sheetProfileEntities" : qUnion([Q0]) }, { "sheetProfileEntities" : qUnion([Q1]) }], "matchConnections" : true, "connections" : [{ "connectionEntities" : qUnion([Q2, Q3]), "connectionEdgeQueries" : qUnion([]), "connectionEdgeParameters" : [] }]});
        }
        {
            var Q0;
            Q0=makeQuery(id+"F24.opLoft","CAP_FACE",FACE,{"disambiguationData":[OSD([makeQuery(id+"F23.imprint","IMPRINT",FACE,{"disambiguationData":[TD([[makeQuery(id+"F23.imprint","IMPRINT",EDGE,{"derivedFrom":sQuery(id+"F23.wireOp",EDGE,"E150.rect.bottom")}),-1.0]])]})])],"isStart":true});
            fillet(context, id + "F25", {"entities" : qUnion([Q0]), "radius" : 1.5 * mm, "tangentPropagation" : true, "allowEdgeOverflow" : false});
        }
        {
            var Q0;
            Q0 = qSketchRegion(id + "F17", true);
            extrude(context, id + "F26", {"entities" : qUnion([Q0]), "operationType" : NewBodyOperationType.REMOVE, "endBound" : BoundingType.SYMMETRIC, "oppositeDirection" : true, "depth" : 25 * mm});
        }
        {
            var Q0;
            Q0=qCreatedBy(makeId("Right.planeOp"),FACE);
            var sketch = newSketch(context, id + "F27", { "sketchPlane" : qUnion([Q0])});
            skLineSegment(sketch, "E155.0", {"start": v(-12, -4.15) * mm, "end": v(-12, 0.9) * mm});
            skLineSegment(sketch, "E156", {"start": v(-12, -2.15) * mm, "end": v(-15, -2.15) * mm});
            skLineSegment(sketch, "E157", {"start": v(-15, -2.15) * mm, "end": v(-15, -0.65) * mm});
            skLineSegment(sketch, "E158", {"start": v(-15, -0.65) * mm, "end": v(-18, -0.65) * mm});
            skLineSegment(sketch, "E159", {"start": v(-18, -0.65) * mm, "end": v(-18, -4.15) * mm});
            skLineSegment(sketch, "E160", {"start": v(-18, -4.15) * mm, "end": v(-12, -4.15) * mm});
            skSolve(sketch);
        }
        {
            var Q0;
            Q0=makeQuery(id+"F21.opLoft","SWEPT_BODY",BODY,{"disambiguationData":[OSD([makeQuery(id+"F19.imprint","IMPRINT",FACE,{"disambiguationData":[TD([[makeQuery(id+"F19.imprint","IMPRINT",EDGE,{"derivedFrom":sQuery(id+"F19.wireOp",EDGE,"E135.0")}),1.0]])]}),makeQuery(id+"F20.imprint","IMPRINT",FACE,{"disambiguationData":[TD([[makeQuery(id+"F20.imprint","IMPRINT",EDGE,{"derivedFrom":sQuery(id+"F20.wireOp",EDGE,"E141")}),1.0]])]})])]});
            var Q1;
            Q1=makeQuery(id+"F24.opLoft","SWEPT_BODY",BODY,{"disambiguationData":[OSD([makeQuery(id+"F19.imprint","IMPRINT",FACE,{"disambiguationData":[TD([[makeQuery(id+"F19.imprint","IMPRINT",EDGE,{"derivedFrom":sQuery(id+"F19.wireOp",EDGE,"E135.0")}),1.0]])]}),makeQuery(id+"F23.imprint","IMPRINT",FACE,{"disambiguationData":[TD([[makeQuery(id+"F23.imprint","IMPRINT",EDGE,{"derivedFrom":sQuery(id+"F23.wireOp",EDGE,"E150.rect.bottom")}),-1.0]])]})])]});
            transform(context, id + "F28", {"entities" : qUnion([Q0, Q1]), "transformType" : TransformType.TRANSLATION_3D, "dx" : 0 * mm, "dy" : 0 * mm, "dz" : 0 * mm, "makeCopy" : true});
        }
        {
            var Q0;
            Q0 = qSketchRegion(id + "F27", true);
            extrude(context, id + "F29", {"entities" : qUnion([Q0]), "operationType" : NewBodyOperationType.INTERSECT, "endBound" : BoundingType.SYMMETRIC, "oppositeDirection" : true, "depth" : 25 * mm});
        }
        {
            var Q0;
            Q0 = qSketchRegion(id + "F27", true);
            extrude(context, id + "F30", {"entities" : qUnion([Q0]), "operationType" : NewBodyOperationType.INTERSECT, "endBound" : BoundingType.SYMMETRIC, "oppositeDirection" : true, "depth" : 25 * mm});
        }
        {
            var Q0;
            Q0=makeQuery(id+"F21.opLoft","SWEPT_BODY",BODY,{"disambiguationData":[OSD([makeQuery(id+"F19.imprint","IMPRINT",FACE,{"disambiguationData":[TD([[makeQuery(id+"F19.imprint","IMPRINT",EDGE,{"derivedFrom":sQuery(id+"F19.wireOp",EDGE,"E135.0")}),1.0]])]}),makeQuery(id+"F20.imprint","IMPRINT",FACE,{"disambiguationData":[TD([[makeQuery(id+"F20.imprint","IMPRINT",EDGE,{"derivedFrom":sQuery(id+"F20.wireOp",EDGE,"E141")}),1.0]])]})])]});
            var Q1;
            Q1=makeQuery(id+"F28.opPattern","COPY",BODY,{"derivedFrom":makeQuery(id+"F21.opLoft","SWEPT_BODY",BODY,{"disambiguationData":[OSD([makeQuery(id+"F19.imprint","IMPRINT",FACE,{"disambiguationData":[TD([[makeQuery(id+"F19.imprint","IMPRINT",EDGE,{"derivedFrom":sQuery(id+"F19.wireOp",EDGE,"E135.0")}),1.0]])]}),makeQuery(id+"F20.imprint","IMPRINT",FACE,{"disambiguationData":[TD([[makeQuery(id+"F20.imprint","IMPRINT",EDGE,{"derivedFrom":sQuery(id+"F20.wireOp",EDGE,"E141")}),1.0]])]})])]}),"instanceName":"1"});
            booleanBodies(context, id + "F31", {"operationType" : BooleanOperationType.SUBTRACTION, "tools" : qUnion([Q0]), "targets" : qUnion([Q1]), "offset" : true, "offsetAll" : true, "offsetDistance" : 0.1 * mm, "keepTools" : true});
        }
        {
            var Q0;
            Q0=makeQuery(id+"F24.opLoft","SWEPT_BODY",BODY,{"disambiguationData":[OSD([makeQuery(id+"F19.imprint","IMPRINT",FACE,{"disambiguationData":[TD([[makeQuery(id+"F19.imprint","IMPRINT",EDGE,{"derivedFrom":sQuery(id+"F19.wireOp",EDGE,"E135.0")}),1.0]])]}),makeQuery(id+"F23.imprint","IMPRINT",FACE,{"disambiguationData":[TD([[makeQuery(id+"F23.imprint","IMPRINT",EDGE,{"derivedFrom":sQuery(id+"F23.wireOp",EDGE,"E150.rect.bottom")}),-1.0]])]})])]});
            var Q1;
            Q1=makeQuery(id+"F28.opPattern","COPY",BODY,{"derivedFrom":makeQuery(id+"F24.opLoft","SWEPT_BODY",BODY,{"disambiguationData":[OSD([makeQuery(id+"F19.imprint","IMPRINT",FACE,{"disambiguationData":[TD([[makeQuery(id+"F19.imprint","IMPRINT",EDGE,{"derivedFrom":sQuery(id+"F19.wireOp",EDGE,"E135.0")}),1.0]])]}),makeQuery(id+"F23.imprint","IMPRINT",FACE,{"disambiguationData":[TD([[makeQuery(id+"F23.imprint","IMPRINT",EDGE,{"derivedFrom":sQuery(id+"F23.wireOp",EDGE,"E150.rect.bottom")}),-1.0]])]})])]}),"instanceName":"1"});
            booleanBodies(context, id + "F32", {"operationType" : BooleanOperationType.SUBTRACTION, "tools" : qUnion([Q0]), "targets" : qUnion([Q1]), "offset" : true, "offsetAll" : true, "offsetDistance" : 0.1 * mm});
        }
        {
            var Q0;
            Q0=sQuery(id+"F1.wireOp",VERTEX,"E64");
            var Q1;
            Q1=qCreatedBy(makeId("Front.planeOp"),FACE);
            cPlane(context, id + "F33", {"entities" : qUnion([Q0, Q1]), "cplaneType" : CPlaneType.PLANE_POINT, "offset" : 150 * mm, "width" : 150 * mm, "height" : 150 * mm});
        }
        {
            var Q0;
            Q0=makeQuery(id+"F21.opLoft","SWEPT_BODY",BODY,{"disambiguationData":[OSD([makeQuery(id+"F19.imprint","IMPRINT",FACE,{"disambiguationData":[TD([[makeQuery(id+"F19.imprint","IMPRINT",EDGE,{"derivedFrom":sQuery(id+"F19.wireOp",EDGE,"E135.0")}),1.0]])]}),makeQuery(id+"F20.imprint","IMPRINT",FACE,{"disambiguationData":[TD([[makeQuery(id+"F20.imprint","IMPRINT",EDGE,{"derivedFrom":sQuery(id+"F20.wireOp",EDGE,"E141")}),1.0]])]})])]});
            var Q1;
            Q1=makeQuery(id+"F28.opPattern","COPY",BODY,{"derivedFrom":makeQuery(id+"F21.opLoft","SWEPT_BODY",BODY,{"disambiguationData":[OSD([makeQuery(id+"F19.imprint","IMPRINT",FACE,{"disambiguationData":[TD([[makeQuery(id+"F19.imprint","IMPRINT",EDGE,{"derivedFrom":sQuery(id+"F19.wireOp",EDGE,"E135.0")}),1.0]])]}),makeQuery(id+"F20.imprint","IMPRINT",FACE,{"disambiguationData":[TD([[makeQuery(id+"F20.imprint","IMPRINT",EDGE,{"derivedFrom":sQuery(id+"F20.wireOp",EDGE,"E141")}),1.0]])]})])]}),"instanceName":"1"});
            var Q2;
            Q2=qCreatedBy(id+"F33.planeOp",FACE);
            mirror(context, id + "F34", {"entities" : qUnion([Q0, Q1]), "mirrorPlane" : qUnion([Q2])});
        }
    });
